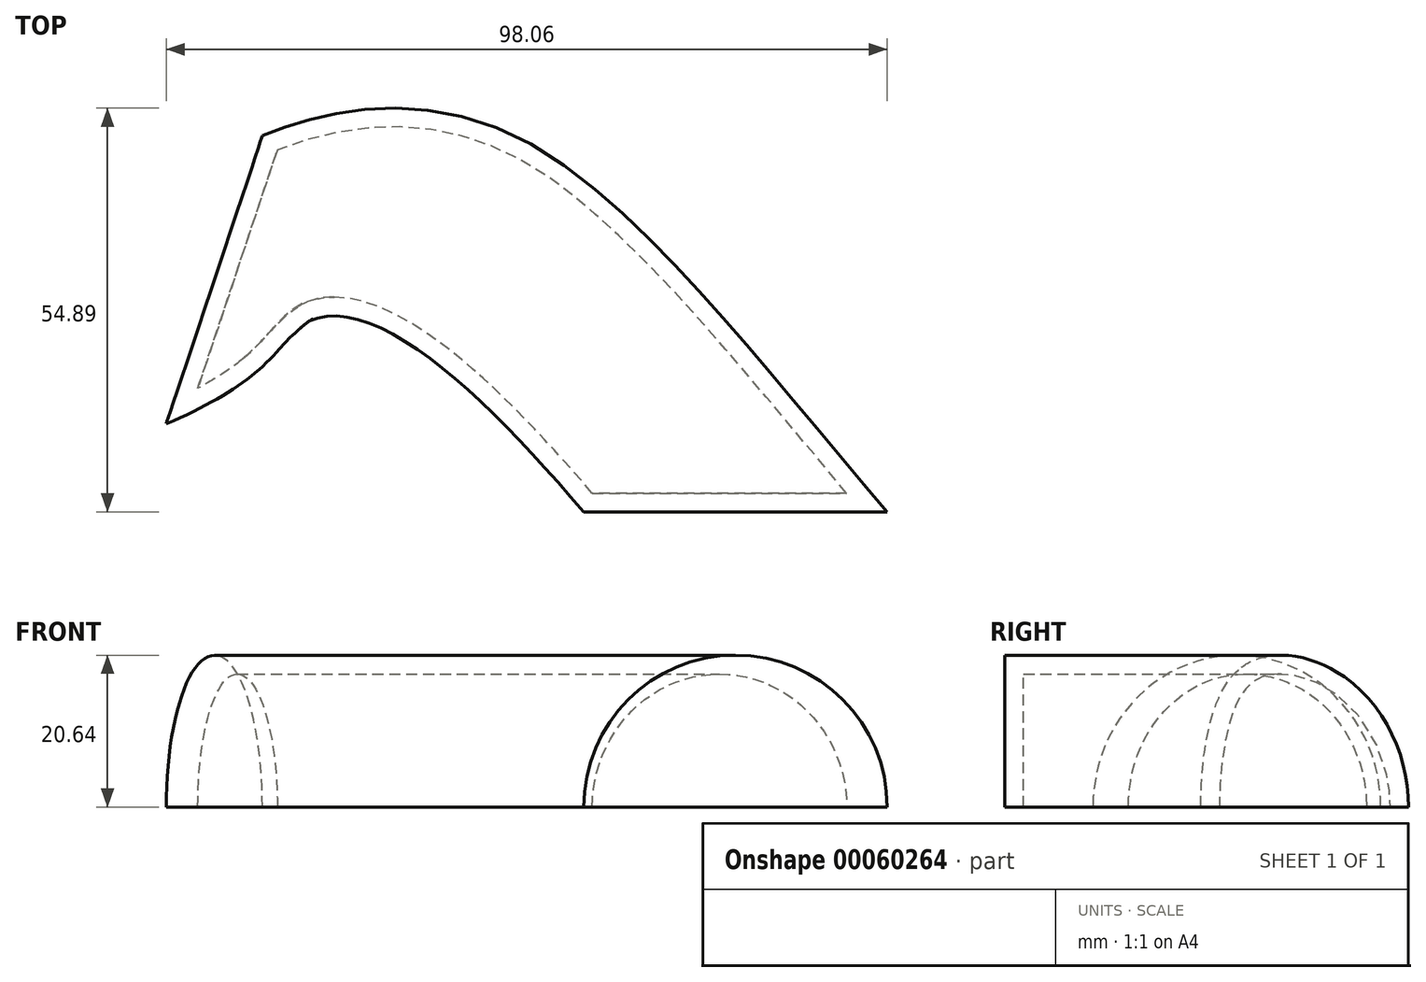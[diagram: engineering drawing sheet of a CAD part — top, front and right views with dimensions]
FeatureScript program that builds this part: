
annotation { "Feature Type Name" : "Feature", "Feature Type Description" : "" }
export const myFeature = defineFeature(function(context is Context, id is Id, definition is map)
    precondition{}
    {
        {
            var Q0;
            Q0=qCreatedBy(makeId("Front.planeOp"),FACE);
            var sketch = newSketch(context, id + "F0", { "sketchPlane" : qUnion([Q0])});
            skLineSegment(sketch, "E0", {"start": v(-20.64, 0) * mm, "end": v(20.64, 0) * mm});
            skArc(sketch, "E1", {"start": v(20.64, 0) * mm, "mid": v(0, 20.64) * mm, "end": v(-20.64, 0) * mm});
            skSolve(sketch);
        }
        {
            var Q0;
            Q0=qCreatedBy(makeId("Top.planeOp"),FACE);
            var sketch = newSketch(context, id + "F1", { "sketchPlane" : qUnion([Q0])});
            skFitSpline(sketch, "E2", {"points": [v(0, 0) * mm, v(-41.87, 36.64) * mm, v(-70.89, 31.55) * mm], "startDerivative": vector(-73.34, 85.1) * mm, "endDerivative": vector(-68.16, -27.94) * mm});
            skSolve(sketch);
        }
        {
            var Q0;
            Q0=makeQuery(id+"F0.imprint","IMPRINT",FACE,{"disambiguationData":[TD([[makeQuery(id+"F0.imprint","IMPRINT",EDGE,{"derivedFrom":sQuery(id+"F0.wireOp",EDGE,"E0")}),1.0]])]});
            var Q1;
            Q1=sQuery(id+"F1.wireOp",EDGE,"E2");
            sweep(context, id + "F2", {"profiles" : qUnion([Q0]), "path" : qUnion([Q1])});
        }
        {
            var Q0;
            Q0=makeQuery(id+"F2.opSweep","SWEPT_FACE",FACE,{"disambiguationData":[OSD([sQuery(id+"F0.wireOp",EDGE,"E0"),sQuery(id+"F1.wireOp",EDGE,"E2")])]});
            shell(context, id + "F3", {"entities" : qUnion([Q0]), "thickness" : 2.54 * mm});
        }
    });
